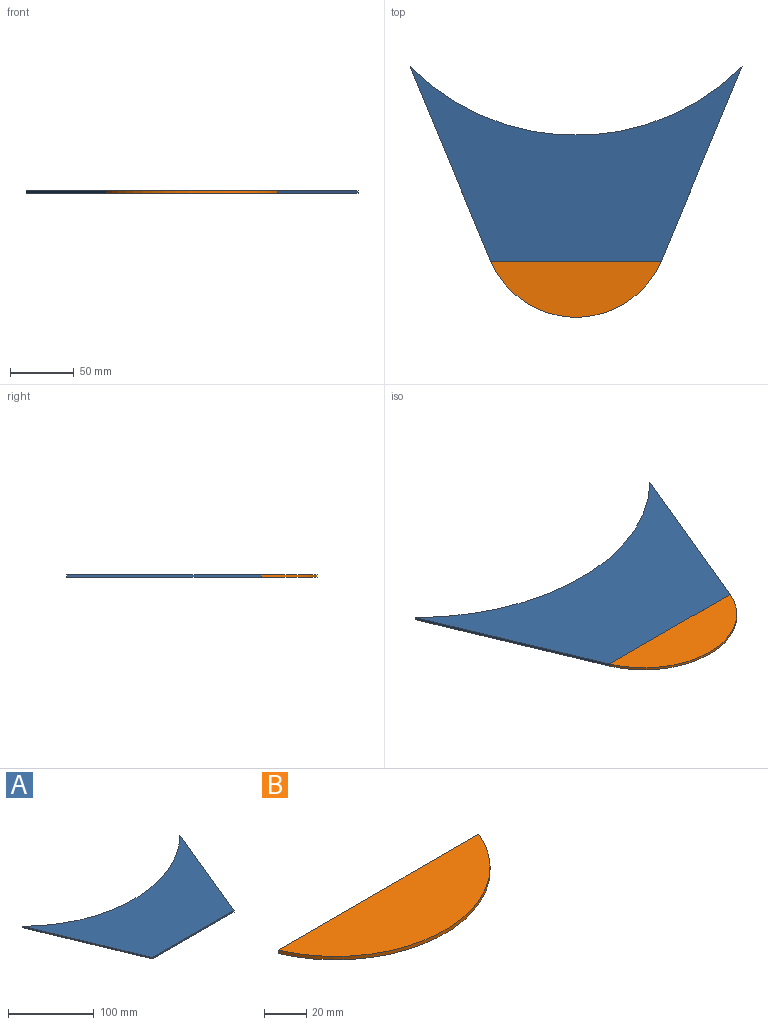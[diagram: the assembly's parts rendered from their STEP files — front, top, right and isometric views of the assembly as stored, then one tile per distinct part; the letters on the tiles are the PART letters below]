
ASSEMBLY  parts=2 mates=1
PART A: 6 faces, bbox 261x152.6x2 mm
  f0: plane 152.65x63.43mm, normal (0.92,-0.38,0), area 330.6mm2, adj f1,f3,f4,f5
  f1: plane 134.14x2mm, normal (0,-1,0), area 268.3mm2, adj f0,f2,f4,f5
  f2: plane 152.65x63.43mm, normal (-0.92,-0.38,0), area 330.6mm2, adj f1,f3,f4,f5
  f3: cylinder r=185mm len=261mm, axis (0,0,1), area 579.4mm2, adj f0,f2,f4,f5
  f4: plane 261x152.65mm, normal (0,0,-1), area 20473.2mm2, adj f0,f1,f2,f3
  f5: plane 261x152.65mm, normal (0,0,1), area 20473.2mm2, adj f0,f1,f2,f3
PART B: 4 faces, bbox 134.1x44.2x2 mm
  f0: plane 134.13x2mm, normal (0,1,0), area 268.3mm2, adj f1,f2,f3
  f1: cylinder r=72.98mm len=134.13mm, axis (0,0,1), area 340.2mm2, adj f0,f2,f3
  f2: plane 134.13x44.2mm, normal (0,0,-1), area 4277.3mm2, adj f0,f1
  f3: plane 134.13x44.2mm, normal (0,0,1), area 4277.3mm2, adj f0,f1
PLACE A t=(0,16.2,98)mm
PLACE B t=(0,16.2,98)mm
MATE fastened A.f5 <-> B.f3  axis (0,0,1) through (0,-62.58,0)mm
